# Revit family: IS_CeraplanNew_B4099_BIM_NL
name_source: partatom
category: Plumbing Fixtures
revit_build: Autodesk Revit 2017 (Build: 20171027_0315(x64)
units: mm (PartAtom-declared; Revit-internal decimal feet)

## family parameters
Cut with Voids When Loaded = No
Host = Face
OmniClass Number = 23.45.55.17
OmniClass Title = Mixing Faucets
Part Type = Normal
Room Calculation Point = No
Round Connector Dimension = Use Diameter
Shared = Yes

## types (1)
- B4099AA - CERAPLAN WASTAFELMENGKRAAN Z/WASTE CHR
    Accessories = www.idealstandardnederland.nl
    AreaUnits = millimeters
    Assembly Code = C1030200
    AssetType = Fixed
    BIMObjectName = Wastafelmengkraan
    BREEAMApproved = No
    BarCode = 3800019243446
    Brand = Ideal Standard
    CWFU = 0
    CodePerformance = EN 817, DIN 4109
    Color = Chroom
    ConnectionType = Sanitair
    Cost = 0 $
    Default Elevation = 0 mm  [stored 0 ft]
    Description = CeraPlan wastafelmengkraan DN 15. Vaste gegoten uitloop. Straalregelaar. Zonder waste. Sprong 117 mm. Hoogte uitloop 42 mm. Flexibele aansluitslangen G3/8". Metalen greep. EASY FIX Onderbevestiging. CLICK 50% Volumestop. Bevestiging greep op de cartouche d.m.v. een RVS overbrengingspen. Draaibereik 120°. Drukafhankelijke temperatuur instelling. Geïntegreerd vetreservoir. Uithoudingstest EN 817. Geluidsniveau volgens norm DIN 4109, Groep 1.
    DurationUnit = year
    ECA = No
    ExpectedLife = 30
    FaucetFunction = Mengkraan
    FaucetOperation = Eenhendel
    FaucetType = Wastafelmengkraan
    Features = Wastafelmengkraan DN 15. Vaste gegoten uitloop. Straalregelaar. Zonder waste. Sprong 117 mm. Hoogte uitloop 42 mm. Flexibele aansluitslangen G3/8". Metalen greep. EASY FIX Onderbevestiging. CLICK 50% Volumestop. Bevestiging greep op de cartouche d.m.v. een RVS overbrengingspen. Draaibereik 120°. Drukafhankelijke temperatuur instelling. Geïntegreerd vetreservoir. Uithoudingstest EN 817. Geluidsniveau volgens norm DIN 4109, Groep 1.
    Finish = Chroom
    FlowRate = 9 liter @ 3 bar
    HWFU = 0
    IfcExportAs = IfcValveType
    IfcExportType = FAUCET
    InstallationInstructions = http://www.idealstandardnederland.nl
    LinearUnits = millimeters
    ManufacturerURL = www.idealstandardnederland.nl
    Material = Messing
    Model = B4099AA
    ModelNumber = B4099AA
    ModelReference = CeraPlan wastafelmengkraan DN 15. Vaste gegoten uitloop. Straalregelaar. Zonder waste. Sprong 117 mm. Hoogte uitloop 42 mm. Flexibele aansluitslangen G3/8". Metalen greep. EASY FIX Onderbevestiging. CLICK 50% Volumestop. Bevestiging greep op de cartouche d.m.v. een RVS overbrengingspen. Draaibereik 120°. Drukafhankelijke temperatuur instelling. Geïntegreerd vetreservoir. Uithoudingstest EN 817. Geluidsniveau volgens norm DIN 4109, Groep 1.
    NBSReference = 45-35-70/???
    Name = CERAPLAN WASTAFELMENGKRAAN Z/WASTE CHR
    NettWeight = 1,39 kg
    NominalHeight = 137 mm
    NominalLength = 165 mm
    NominalWidth = 56 mm
    ProductInformation = http://www.idealstandardnederland.nl
    Shape = Sculptured
    Size = 56 x 165 x 137 mm
    Space = Internal
    SpareParts = www.idealstandardnederland.nl
    TMV3 = Yes
    TestPressure = 10 Bar
    URL = www.idealspec.nl
    Uniclass2015Code = Pr_40_20_87_96
    Uniclass2015Title = Washbasin manual water supply sets
    ValveMechanism = Keramische schijven
    ValveOperation = Eenhendel
    Version = 2
    VolumeUnits = Liter
    WFU = 0
    WRAS = Yes
    WarrantyDescription = Fabrieksgarantie
    WarrantyDurationParts = 10
    WarrantyDurationUnit = jaar
    WaterEfficientProduct = No
    WorkingPressure = 1-5 bar

note: [stored X ft] marks values corroborated as IEEE doubles in the binary element streams (Revit-internal decimal feet)

## geometry (parser evidence)
native form markers: Sweep x1
no freeform markers — native parametric forms only
